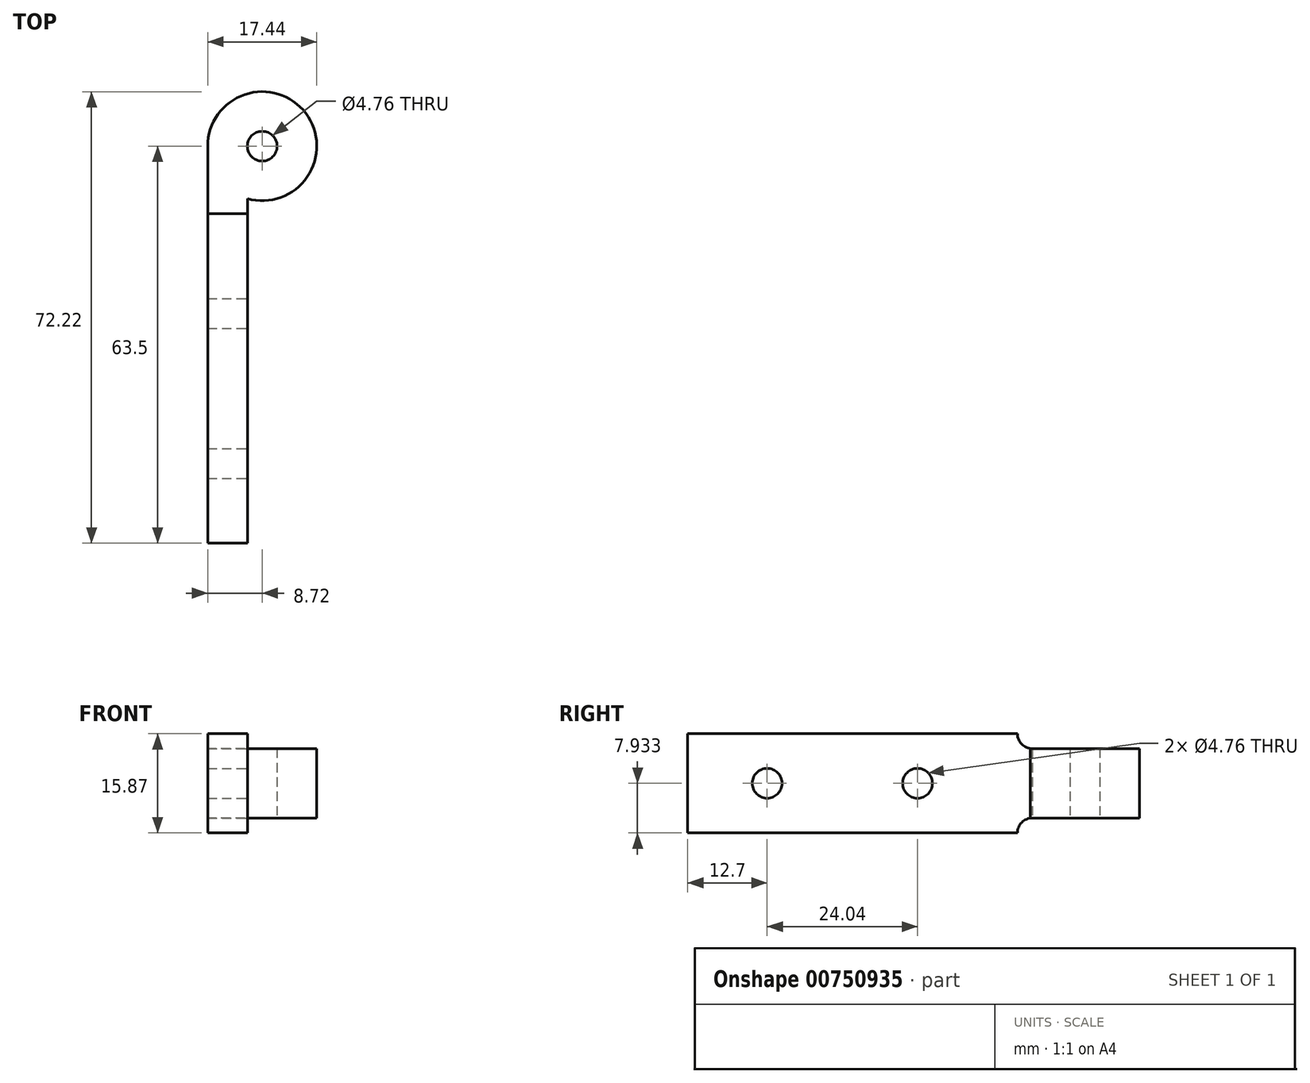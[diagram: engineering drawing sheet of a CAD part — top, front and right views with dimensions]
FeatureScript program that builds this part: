
annotation { "Feature Type Name" : "Feature", "Feature Type Description" : "" }
export const myFeature = defineFeature(function(context is Context, id is Id, definition is map)
    precondition{}
    {
        {
            var Q0;
            Q0=qCreatedBy(makeId("Top.planeOp"),FACE);
            var sketch = newSketch(context, id + "F0", { "sketchPlane" : qUnion([Q0])});
            skCircle(sketch, "E0", {"center": v(0, 0) * mm, "radius": 8.72 * mm});
            skCircle(sketch, "E1", {"center": v(0, 0) * mm, "radius": 2.38 * mm});
            skSolve(sketch);
        }
        {
            var Q0;
            Q0=makeQuery(id+"F0.imprint","IMPRINT",FACE,{"disambiguationData":[TD([[makeQuery(id+"F0.imprint","IMPRINT",EDGE,{"derivedFrom":sQuery(id+"F0.wireOp",EDGE,"E0")}),1.0]])]});
            extrude(context, id + "F1", {"entities" : qUnion([Q0]), "depth" : 9.52 * mm, "offsetDistance" : 25.4 * mm});
        }
        {
            var Q0;
            Q0=makeQuery(id+"F1.opExtrude","CAP_FACE",FACE,{"disambiguationData":[OSD([sQuery(id+"F0.wireOp",EDGE,"E0"),sQuery(id+"F0.wireOp",EDGE,"E1")])],"isStart":true});
            var sketch = newSketch(context, id + "F2", { "sketchPlane" : qUnion([Q0])});
            skLineSegment(sketch, "E2", {"start": v(0, 0) * mm, "end": v(-8.72, 0) * mm, "construction": true});
            skLineSegment(sketch, "E3", {"start": v(-8.72, 0) * mm, "end": v(-8.72, 63.5) * mm});
            skLineSegment(sketch, "E4", {"start": v(-8.72, 63.5) * mm, "end": v(-2.37, 63.5) * mm});
            skLineSegment(sketch, "E5", {"start": v(-2.37, 63.5) * mm, "end": v(-2.37, 8.4) * mm});
            skSolve(sketch);
        }
        {
            var Q0;
            Q0 = qSketchRegion(id + "F2", true);
            var Q1;
            {var subQ0=sQuery(id+"F2.wireOp",EDGE,"E3");Q1=makeQuery(id+"F2.imprint","IMPRINT",FACE,{"disambiguationData":[TD([[makeQuery(id+"F2.imprint","IMPRINT",EDGE,{"derivedFrom":subQ0}),-1.0]])]});}
            extrude(context, id + "F3", {"entities" : qUnion([Q0, Q1]), "operationType" : NewBodyOperationType.ADD, "oppositeDirection" : true, "depth" : 9.52 * mm, "offsetDistance" : 25.4 * mm});
        }
        {
            var Q0;
            Q0=makeQuery(id+"F3.opExtrude","SWEPT_FACE",FACE,{"disambiguationData":[OSD([sQuery(id+"F2.wireOp",EDGE,"E5")])]});
            var sketch = newSketch(context, id + "F4", { "sketchPlane" : qUnion([Q0])});
            skLineSegment(sketch, "E6", {"start": v(-63.5, 4.76) * mm, "end": v(-50.8, 4.76) * mm});
            skLineSegment(sketch, "E7", {"start": v(-8.4, 4.76) * mm, "end": v(-26.76, 4.76) * mm});
            skCircle(sketch, "E8", {"center": v(-50.8, 4.76) * mm, "radius": 2.38 * mm});
            skCircle(sketch, "E9", {"center": v(-26.76, 4.76) * mm, "radius": 2.38 * mm});
            skSolve(sketch);
        }
        {
            var Q0;
            Q0 = qSketchRegion(id + "F4", true);
            extrude(context, id + "F5", {"entities" : qUnion([Q0]), "operationType" : NewBodyOperationType.REMOVE, "oppositeDirection" : true, "depth" : 25.4 * mm, "offsetDistance" : 25.4 * mm});
        }
        {
            var Q0;
            {var subQ0=sQuery(id+"F0.wireOp",EDGE,"E0");Q0=makeQuery(id+"F3.boolean.opBoolean","MERGE",FACE,{"derivedFrom":[makeQuery(id+"F1.opExtrude","CAP_FACE",FACE,{"disambiguationData":[OSD([subQ0,sQuery(id+"F0.wireOp",EDGE,"E1")])],"isStart":false}),makeQuery(id+"F3.opExtrude","CAP_FACE",FACE,{"disambiguationData":[OSD([subQ0,sQuery(id+"F2.wireOp",EDGE,"E3"),sQuery(id+"F2.wireOp",EDGE,"E4"),sQuery(id+"F2.wireOp",EDGE,"E5")])],"isStart":false})]});}
            var sketch = newSketch(context, id + "F6", { "sketchPlane" : qUnion([Q0])});
            skArc(sketch, "E10.0.0", {"start": v(-2.37, -8.4) * mm, "mid": v(6.96, 5.26) * mm, "end": v(-8.72, 0) * mm});
            skLineSegment(sketch, "E10.0.1", {"start": v(-8.72, 0) * mm, "end": v(-8.72, -63.5) * mm});
            skLineSegment(sketch, "E10.0.2", {"start": v(-8.72, -63.5) * mm, "end": v(-2.37, -63.5) * mm});
            skLineSegment(sketch, "E10.0.3", {"start": v(-2.37, -63.5) * mm, "end": v(-2.37, -8.4) * mm});
            skLineSegment(sketch, "E11", {"start": v(-2.37, -8.4) * mm, "end": v(-8.72, -8.4) * mm});
            skSolve(sketch);
        }
        {
            var Q0;
            {var subQ0=sQuery(id+"F6.wireOp",EDGE,"E10.0.2");Q0=makeQuery(id+"F6.imprint","IMPRINT",FACE,{"disambiguationData":[TD([[makeQuery(id+"F6.imprint","IMPRINT",EDGE,{"derivedFrom":subQ0}),1.0]])]});}
            extrude(context, id + "F7", {"entities" : qUnion([Q0]), "operationType" : NewBodyOperationType.ADD, "depth" : 3.17 * mm, "offsetDistance" : 25.4 * mm});
        }
        {
            var Q0;
            {var subQ0=sQuery(id+"F0.wireOp",EDGE,"E0");Q0=makeQuery(id+"F3.boolean.opBoolean","MERGE",FACE,{"derivedFrom":[makeQuery(id+"F1.opExtrude","CAP_FACE",FACE,{"disambiguationData":[OSD([subQ0,sQuery(id+"F0.wireOp",EDGE,"E1")])],"isStart":true}),makeQuery(id+"F3.opExtrude","CAP_FACE",FACE,{"disambiguationData":[OSD([subQ0,sQuery(id+"F2.wireOp",EDGE,"E3"),sQuery(id+"F2.wireOp",EDGE,"E4"),sQuery(id+"F2.wireOp",EDGE,"E5")])],"isStart":true})]});}
            var sketch = newSketch(context, id + "F8", { "sketchPlane" : qUnion([Q0])});
            skLineSegment(sketch, "E12.0", {"start": v(-8.72, 0) * mm, "end": v(-8.72, 63.5) * mm});
            skArc(sketch, "E13.0.0", {"start": v(-8.72, 0) * mm, "mid": v(6.96, -5.26) * mm, "end": v(-2.37, 8.4) * mm});
            skLineSegment(sketch, "E13.0.1", {"start": v(-2.37, 8.4) * mm, "end": v(-2.37, 63.5) * mm});
            skLineSegment(sketch, "E13.0.2", {"start": v(-2.37, 63.5) * mm, "end": v(-8.72, 63.5) * mm});
            skLineSegment(sketch, "E13.0.3", {"start": v(-8.72, 63.5) * mm, "end": v(-8.72, 0) * mm});
            skLineSegment(sketch, "E14", {"start": v(-2.37, 8.4) * mm, "end": v(-8.72, 8.4) * mm});
            skSolve(sketch);
        }
        {
            var Q0;
            Q0=makeQuery(id+"F8.imprint","IMPRINT",FACE,{"disambiguationData":[TD([[makeQuery(id+"F8.imprint","IMPRINT",EDGE,{"derivedFrom":sQuery(id+"F8.wireOp",EDGE,"E13.0.1")}),-1.0]])]});
            extrude(context, id + "F9", {"entities" : qUnion([Q0]), "operationType" : NewBodyOperationType.ADD, "depth" : 3.17 * mm, "offsetDistance" : 25.4 * mm});
        }
        {
            var Q0;
            Q0=makeQuery(id+"F9.boolean.opBoolean","MERGE",FACE,{"derivedFrom":[makeQuery(id+"F7.boolean.opBoolean","MERGE",FACE,{"derivedFrom":[makeQuery(id+"F3.opExtrude","SWEPT_FACE",FACE,{"disambiguationData":[OSD([sQuery(id+"F2.wireOp",EDGE,"E5")])]}),makeQuery(id+"F7.opExtrude","SWEPT_FACE",FACE,{"disambiguationData":[OSD([sQuery(id+"F6.wireOp",EDGE,"E10.0.3")])]})]}),makeQuery(id+"F9.opExtrude","SWEPT_FACE",FACE,{"disambiguationData":[OSD([sQuery(id+"F8.wireOp",EDGE,"E13.0.1")])]})]});
            var sketch = newSketch(context, id + "F10", { "sketchPlane" : qUnion([Q0])});
            skLineSegment(sketch, "E15.0.0", {"start": v(-63.5, 12.7) * mm, "end": v(-63.5, -3.17) * mm});
            skLineSegment(sketch, "E15.0.1", {"start": v(-63.5, -3.18) * mm, "end": v(-8.4, -3.18) * mm});
            skLineSegment(sketch, "E15.0.2", {"start": v(-8.4, -3.18) * mm, "end": v(-8.4, 0) * mm});
            skLineSegment(sketch, "E15.0.3", {"start": v(-8.4, 0) * mm, "end": v(-8.4, 9.53) * mm});
            skLineSegment(sketch, "E15.0.4", {"start": v(-8.4, 9.53) * mm, "end": v(-8.4, 12.7) * mm});
            skLineSegment(sketch, "E15.0.5", {"start": v(-8.4, 12.7) * mm, "end": v(-63.5, 12.7) * mm});
            skLineSegment(sketch, "E16", {"start": v(-8.4, 9.53) * mm, "end": v(-8.4, 10.32) * mm});
            skLineSegment(sketch, "E17", {"start": v(-8.4, 0) * mm, "end": v(-8.4, -0.8) * mm});
            skArc(sketch, "E18", {"start": v(-8.4, 10.32) * mm, "mid": v(-10.08, 11.02) * mm, "end": v(-10.78, 12.7) * mm});
            skArc(sketch, "E19", {"start": v(-8.4, -0.8) * mm, "mid": v(-10.08, -1.5) * mm, "end": v(-10.78, -3.17) * mm});
            skSolve(sketch);
        }
        {
            var Q0;
            {var subQ0=sQuery(id+"F10.wireOp",EDGE,"E15.0.2");Q0=makeQuery(id+"F10.imprint","IMPRINT",FACE,{"disambiguationData":[TD([[makeQuery(id+"F10.imprint","IMPRINT",EDGE,{"derivedFrom":subQ0}),1.0]])]});}
            var Q1;
            {var subQ0=sQuery(id+"F10.wireOp",EDGE,"E15.0.4");Q1=makeQuery(id+"F10.imprint","IMPRINT",FACE,{"disambiguationData":[TD([[makeQuery(id+"F10.imprint","IMPRINT",EDGE,{"derivedFrom":subQ0}),-1.0]])]});}
            extrude(context, id + "F11", {"entities" : qUnion([Q0, Q1]), "operationType" : NewBodyOperationType.REMOVE, "oppositeDirection" : true, "depth" : 25.4 * mm, "offsetDistance" : 25.4 * mm});
        }
        {
            var Q0;
            {var subQ0=sQuery(id+"F0.wireOp",EDGE,"E0");Q0=makeQuery(id+"F3.boolean.opBoolean","MERGE",FACE,{"derivedFrom":[makeQuery(id+"F1.opExtrude","CAP_FACE",FACE,{"disambiguationData":[OSD([subQ0,sQuery(id+"F0.wireOp",EDGE,"E1")])],"isStart":true}),makeQuery(id+"F3.opExtrude","CAP_FACE",FACE,{"disambiguationData":[OSD([subQ0,sQuery(id+"F2.wireOp",EDGE,"E3"),sQuery(id+"F2.wireOp",EDGE,"E4"),sQuery(id+"F2.wireOp",EDGE,"E5")])],"isStart":true})]});}
            extrude(context, id + "F12", {"entities" : qUnion([Q0]), "operationType" : NewBodyOperationType.ADD, "depth" : 0.8 * mm, "offsetDistance" : 25.4 * mm});
        }
        {
            var Q0;
            {var subQ0=sQuery(id+"F0.wireOp",EDGE,"E0");Q0=makeQuery(id+"F3.boolean.opBoolean","MERGE",FACE,{"derivedFrom":[makeQuery(id+"F1.opExtrude","CAP_FACE",FACE,{"disambiguationData":[OSD([subQ0,sQuery(id+"F0.wireOp",EDGE,"E1")])],"isStart":false}),makeQuery(id+"F3.opExtrude","CAP_FACE",FACE,{"disambiguationData":[OSD([subQ0,sQuery(id+"F2.wireOp",EDGE,"E3"),sQuery(id+"F2.wireOp",EDGE,"E4"),sQuery(id+"F2.wireOp",EDGE,"E5")])],"isStart":false})]});}
            extrude(context, id + "F13", {"entities" : qUnion([Q0]), "operationType" : NewBodyOperationType.ADD, "depth" : 0.8 * mm, "offsetDistance" : 25.4 * mm});
        }
    });
